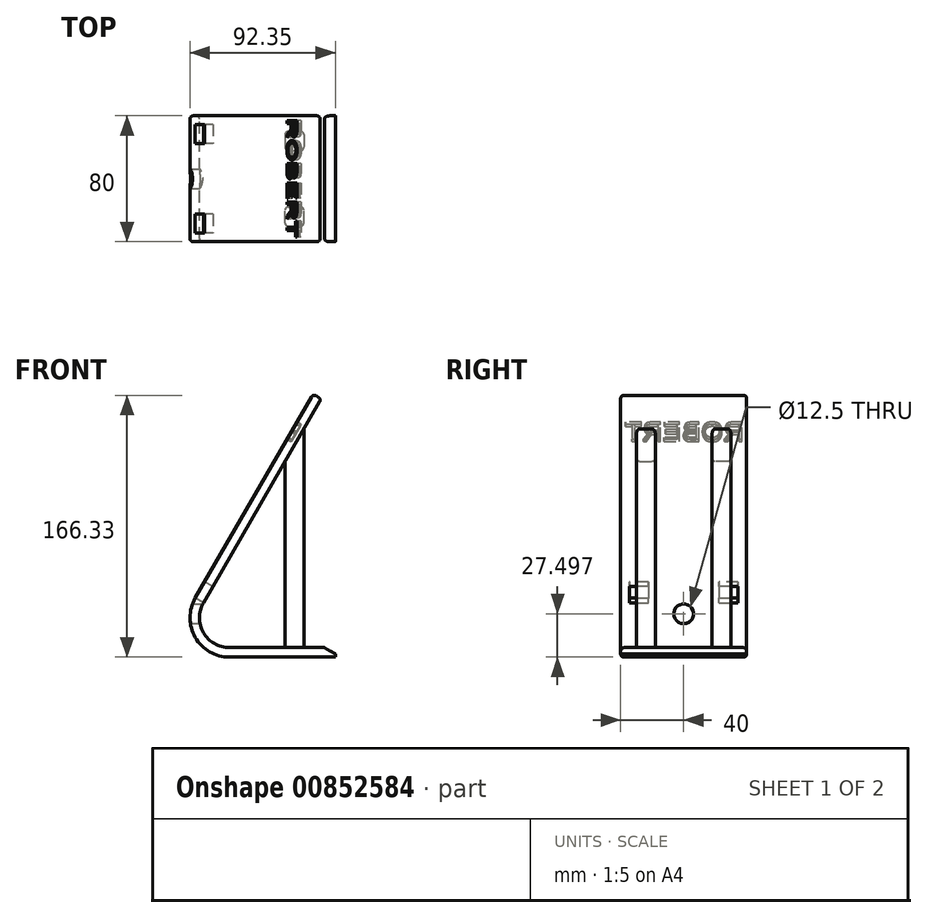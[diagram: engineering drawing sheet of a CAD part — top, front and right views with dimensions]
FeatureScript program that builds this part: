
annotation { "Feature Type Name" : "Feature", "Feature Type Description" : "" }
export const myFeature = defineFeature(function(context is Context, id is Id, definition is map)
    precondition{}
    {
        {
            var Q0;
            Q0=qCreatedBy(makeId("Front.planeOp"),FACE);
            var sketch = newSketch(context, id + "F0", { "sketchPlane" : qUnion([Q0])});
            skLineSegment(sketch, "E0", {"start": v(82.17, -45.58) * mm, "end": v(14.82, -45.58) * mm});
            skLineSegment(sketch, "E1", {"start": v(-6.83, -8.08) * mm, "end": v(67.97, 121.48) * mm});
            skPoint(sketch, "E2.visualSharp", {"position": v(-28.49, -45.58) * mm});
            skArc(sketch, "E2.filletArc", {"start": v(-6.83, -8.08) * mm, "mid": v(-6.83, -33.08) * mm, "end": v(14.82, -45.58) * mm});
            skLineSegment(sketch, "E3.0", {"start": v(-1.64, -11.08) * mm, "end": v(73.17, 118.48) * mm});
            skArc(sketch, "E3.1", {"start": v(-1.64, -11.08) * mm, "mid": v(-1.64, -30.08) * mm, "end": v(14.82, -39.58) * mm});
            skLineSegment(sketch, "E3.2", {"start": v(82.17, -39.58) * mm, "end": v(14.82, -39.58) * mm});
            skLineSegment(sketch, "E4", {"start": v(67.97, 121.48) * mm, "end": v(73.17, 118.48) * mm});
            skLineSegment(sketch, "E5", {"start": v(82.17, -39.58) * mm, "end": v(82.17, -45.58) * mm});
            skSolve(sketch);
        }
        {
            var Q0;
            Q0 = qSketchRegion(id + "F0", true);
            extrude(context, id + "F1", {"entities" : qUnion([Q0]), "depth" : 80 * mm, "offsetDistance" : 25 * mm});
        }
        {
            var Q0;
            Q0=makeQuery(id+"F1.opExtrude","SWEPT_FACE",FACE,{"disambiguationData":[OSD([sQuery(id+"F0.wireOp",EDGE,"E3.2")])]});
            var sketch = newSketch(context, id + "F2", { "sketchPlane" : qUnion([Q0])});
            skLineSegment(sketch, "E6.bottom", {"start": v(50.17, -10) * mm, "end": v(62.17, -10) * mm});
            skLineSegment(sketch, "E6.top", {"start": v(50.17, -22) * mm, "end": v(62.17, -22) * mm});
            skLineSegment(sketch, "E6.left", {"start": v(50.17, -10) * mm, "end": v(50.17, -22) * mm});
            skLineSegment(sketch, "E6.right", {"start": v(62.17, -10) * mm, "end": v(62.17, -22) * mm});
            skLineSegment(sketch, "E7.bottom", {"start": v(50.17, -70) * mm, "end": v(62.17, -70) * mm});
            skLineSegment(sketch, "E7.top", {"start": v(50.17, -58) * mm, "end": v(62.17, -58) * mm});
            skLineSegment(sketch, "E7.left", {"start": v(50.17, -70) * mm, "end": v(50.17, -58) * mm});
            skLineSegment(sketch, "E7.right", {"start": v(62.17, -70) * mm, "end": v(62.17, -58) * mm});
            skSolve(sketch);
        }
        {
            var Q0;
            Q0 = qSketchRegion(id + "F2", true);
            extrude(context, id + "F3", {"entities" : qUnion([Q0]), "operationType" : NewBodyOperationType.ADD, "endBound" : BoundingType.UP_TO_NEXT, "depth" : 25 * mm, "offsetDistance" : 25 * mm});
        }
        {
            var Q0;
            Q0=qCreatedBy(makeId("Right.planeOp"),FACE);
            var sketch = newSketch(context, id + "F4", { "sketchPlane" : qUnion([Q0])});
            skCircle(sketch, "E8", {"center": v(-40, -18.08) * mm, "radius": 13.93 * mm, "construction": true});
            skSolve(sketch);
        }
        {
            var Q0;
            Q0=sQuery(id+"F4.wireOp",VERTEX,"E8.center");
            var Q1;
            Q1=makeQuery(id+"F1.opExtrude","SWEPT_BODY",BODY,{"disambiguationData":[OSD([sQuery(id+"F0.wireOp",EDGE,"E0"),sQuery(id+"F0.wireOp",EDGE,"E1"),sQuery(id+"F0.wireOp",EDGE,"E2.filletArc"),sQuery(id+"F0.wireOp",EDGE,"E3.0"),sQuery(id+"F0.wireOp",EDGE,"E3.1"),sQuery(id+"F0.wireOp",EDGE,"E3.2"),sQuery(id+"F0.wireOp",EDGE,"E4"),sQuery(id+"F0.wireOp",EDGE,"E5")])]});
            hole(context, id + "F5", {"style" : HoleStyle.SIMPLE, "endStyle" : HoleEndStyle.THROUGH, "holeDiameter" : 12.5 * mm, "majorDiameter" : 5 * mm, "isTappedThrough" : true, "tappedDepth" : 12 * mm, "tapClearance" : 3, "startFromSketch" : true, "locations" : qUnion([Q0]), "scope" : qUnion([Q1])});
        }
        {
            var Q0;
            Q0=makeQuery(id+"F1.opExtrude","SWEPT_FACE",FACE,{"disambiguationData":[OSD([sQuery(id+"F0.wireOp",EDGE,"E1")])]});
            var sketch = newSketch(context, id + "F6", { "sketchPlane" : qUnion([Q0])});
            skLineSegment(sketch, "E9.bottom", {"start": v(5.5, 1.58) * mm, "end": v(17.5, 1.58) * mm});
            skLineSegment(sketch, "E9.top", {"start": v(5.5, -10.42) * mm, "end": v(17.5, -10.42) * mm});
            skLineSegment(sketch, "E9.left", {"start": v(5.5, 1.58) * mm, "end": v(5.5, -10.42) * mm});
            skLineSegment(sketch, "E9.right", {"start": v(17.5, 1.58) * mm, "end": v(17.5, -10.42) * mm});
            skLineSegment(sketch, "E10.bottom", {"start": v(62.5, 1.58) * mm, "end": v(74.5, 1.58) * mm});
            skLineSegment(sketch, "E10.top", {"start": v(62.5, -10.42) * mm, "end": v(74.5, -10.42) * mm});
            skLineSegment(sketch, "E10.left", {"start": v(62.5, 1.58) * mm, "end": v(62.5, -10.42) * mm});
            skLineSegment(sketch, "E10.right", {"start": v(74.5, 1.58) * mm, "end": v(74.5, -10.42) * mm});
            skSolve(sketch);
        }
        {
            var Q0;
            Q0 = qSketchRegion(id + "F6", true);
            extrude(context, id + "F7", {"entities" : qUnion([Q0]), "operationType" : NewBodyOperationType.REMOVE, "oppositeDirection" : true, "depth" : 10 * mm, "offsetDistance" : 25 * mm});
        }
        {
            var Q0;
            Q0=makeQuery(id+"F6.imprint","IMPRINT",FACE,{"disambiguationData":[TD([[makeQuery(id+"F6.imprint","IMPRINT",EDGE,{"derivedFrom":sQuery(id+"F6.wireOp",EDGE,"E9.bottom")}),1.0]])]});
            var sketch = newSketch(context, id + "F8", { "sketchPlane" : qUnion([Q0])});
            skText(sketch, "E11", { "text": "ROBERT", "fontName": "Arimo-Regular.ttf"});
            const initialGuessF8  = {"E11": [0.00167, 0.10609, 1, 0, 0.0131]};
            skSetInitialGuess(sketch, initialGuessF8);
            skSolve(sketch);
        }
        {
            var Q0;
            Q0 = qSketchRegion(id + "F8", true);
            extrude(context, id + "F9", {"entities" : qUnion([Q0]), "operationType" : NewBodyOperationType.REMOVE, "oppositeDirection" : true, "depth" : 3 * mm, "offsetDistance" : 25 * mm});
        }
        {
            var Q0;
            Q0=makeQuery(id+"F1.opExtrude","SWEPT_EDGE",EDGE,{"disambiguationData":[OSD([sQuery(id+"F0.wireOp",EDGE,"E3.0"),sQuery(id+"F0.wireOp",EDGE,"E4")])]});
            var Q1;
            Q1=makeQuery(id+"F1.opExtrude","SWEPT_EDGE",EDGE,{"disambiguationData":[OSD([sQuery(id+"F0.wireOp",EDGE,"E1"),sQuery(id+"F0.wireOp",EDGE,"E4")])]});
            var Q2;
            Q2=makeQuery(id+"F3.opExtrude","SWEPT_EDGE",EDGE,{"disambiguationData":[OSD([sQuery(id+"F2.wireOp",EDGE,"E6.bottom"),sQuery(id+"F2.wireOp",EDGE,"E6.right")])]});
            var Q3;
            Q3=makeQuery(id+"F3.opExtrude","SWEPT_EDGE",EDGE,{"disambiguationData":[OSD([sQuery(id+"F2.wireOp",EDGE,"E6.bottom"),sQuery(id+"F2.wireOp",EDGE,"E6.left")])]});
            var Q4;
            Q4=makeQuery(id+"F3.opExtrude","SWEPT_EDGE",EDGE,{"disambiguationData":[OSD([sQuery(id+"F2.wireOp",EDGE,"E6.top"),sQuery(id+"F2.wireOp",EDGE,"E6.right")])]});
            var Q5;
            Q5=makeQuery(id+"F3.opExtrude","SWEPT_EDGE",EDGE,{"disambiguationData":[OSD([sQuery(id+"F2.wireOp",EDGE,"E6.top"),sQuery(id+"F2.wireOp",EDGE,"E6.left")])]});
            var Q6;
            Q6=makeQuery(id+"F3.opExtrude","SWEPT_EDGE",EDGE,{"disambiguationData":[OSD([sQuery(id+"F2.wireOp",EDGE,"E7.top"),sQuery(id+"F2.wireOp",EDGE,"E7.right")])]});
            var Q7;
            Q7=makeQuery(id+"F3.opExtrude","SWEPT_EDGE",EDGE,{"disambiguationData":[OSD([sQuery(id+"F2.wireOp",EDGE,"E7.bottom"),sQuery(id+"F2.wireOp",EDGE,"E7.right")])]});
            var Q8;
            Q8=makeQuery(id+"F3.opExtrude","SWEPT_EDGE",EDGE,{"disambiguationData":[OSD([sQuery(id+"F2.wireOp",EDGE,"E7.bottom"),sQuery(id+"F2.wireOp",EDGE,"E7.left")])]});
            var Q9;
            Q9=makeQuery(id+"F3.opExtrude","SWEPT_EDGE",EDGE,{"disambiguationData":[OSD([sQuery(id+"F2.wireOp",EDGE,"E7.top"),sQuery(id+"F2.wireOp",EDGE,"E7.left")])]});
            fillet(context, id + "F10", {"entities" : qUnion([Q0, Q1, Q2, Q3, Q4, Q5, Q6, Q7, Q8, Q9]), "radius" : 2 * mm, "tangentPropagation" : true, "allowEdgeOverflow" : false});
        }
        {
            var Q0;
            Q0=makeQuery(id+"F1.opExtrude","CAP_EDGE",EDGE,{"disambiguationData":[OSD([sQuery(id+"F0.wireOp",EDGE,"E1")])],"isStart":true});
            var Q1;
            Q1=makeQuery(id+"F1.opExtrude","CAP_EDGE",EDGE,{"disambiguationData":[OSD([sQuery(id+"F0.wireOp",EDGE,"E3.0")])],"isStart":true});
            var Q2;
            Q2=makeQuery(id+"F1.opExtrude","CAP_EDGE",EDGE,{"disambiguationData":[OSD([sQuery(id+"F0.wireOp",EDGE,"E3.1")])],"isStart":true});
            var Q3;
            Q3=makeQuery(id+"F1.opExtrude","CAP_EDGE",EDGE,{"disambiguationData":[OSD([sQuery(id+"F0.wireOp",EDGE,"E3.2")])],"isStart":true});
            var Q4;
            Q4=makeQuery(id+"F1.opExtrude","CAP_EDGE",EDGE,{"disambiguationData":[OSD([sQuery(id+"F0.wireOp",EDGE,"E0")])],"isStart":true});
            var Q5;
            Q5=makeQuery(id+"F1.opExtrude","CAP_EDGE",EDGE,{"disambiguationData":[OSD([sQuery(id+"F0.wireOp",EDGE,"E2.filletArc")])],"isStart":true});
            var Q6;
            Q6=makeQuery(id+"F1.opExtrude","CAP_EDGE",EDGE,{"disambiguationData":[OSD([sQuery(id+"F0.wireOp",EDGE,"E3.0")])],"isStart":false});
            var Q7;
            Q7=makeQuery(id+"F1.opExtrude","CAP_EDGE",EDGE,{"disambiguationData":[OSD([sQuery(id+"F0.wireOp",EDGE,"E1")])],"isStart":false});
            var Q8;
            Q8=makeQuery(id+"F1.opExtrude","CAP_EDGE",EDGE,{"disambiguationData":[OSD([sQuery(id+"F0.wireOp",EDGE,"E2.filletArc")])],"isStart":false});
            var Q9;
            Q9=makeQuery(id+"F1.opExtrude","CAP_EDGE",EDGE,{"disambiguationData":[OSD([sQuery(id+"F0.wireOp",EDGE,"E3.2")])],"isStart":false});
            var Q10;
            Q10=makeQuery(id+"F1.opExtrude","CAP_EDGE",EDGE,{"disambiguationData":[OSD([sQuery(id+"F0.wireOp",EDGE,"E0")])],"isStart":false});
            var Q11;
            Q11=makeQuery(id+"F1.opExtrude","CAP_EDGE",EDGE,{"disambiguationData":[OSD([sQuery(id+"F0.wireOp",EDGE,"E3.1")])],"isStart":false});
            fillet(context, id + "F11", {"entities" : qUnion([Q0, Q1, Q2, Q3, Q4, Q5, Q6, Q7, Q8, Q9, Q10, Q11]), "radius" : 2 * mm, "tangentPropagation" : true, "allowEdgeOverflow" : false});
        }
        {
            var Q0;
            Q0=makeQuery(id+"F1.opExtrude","SWEPT_EDGE",EDGE,{"disambiguationData":[OSD([sQuery(id+"F0.wireOp",EDGE,"E3.2"),sQuery(id+"F0.wireOp",EDGE,"E5")])]});
            chamfer(context, id + "F12", {"entities" : qUnion([Q0]), "chamferType" : ChamferType.OFFSET_ANGLE, "width" : 7 * mm, "oppositeDirection" : false, "angle" : 30 * degree});
        }
    });
